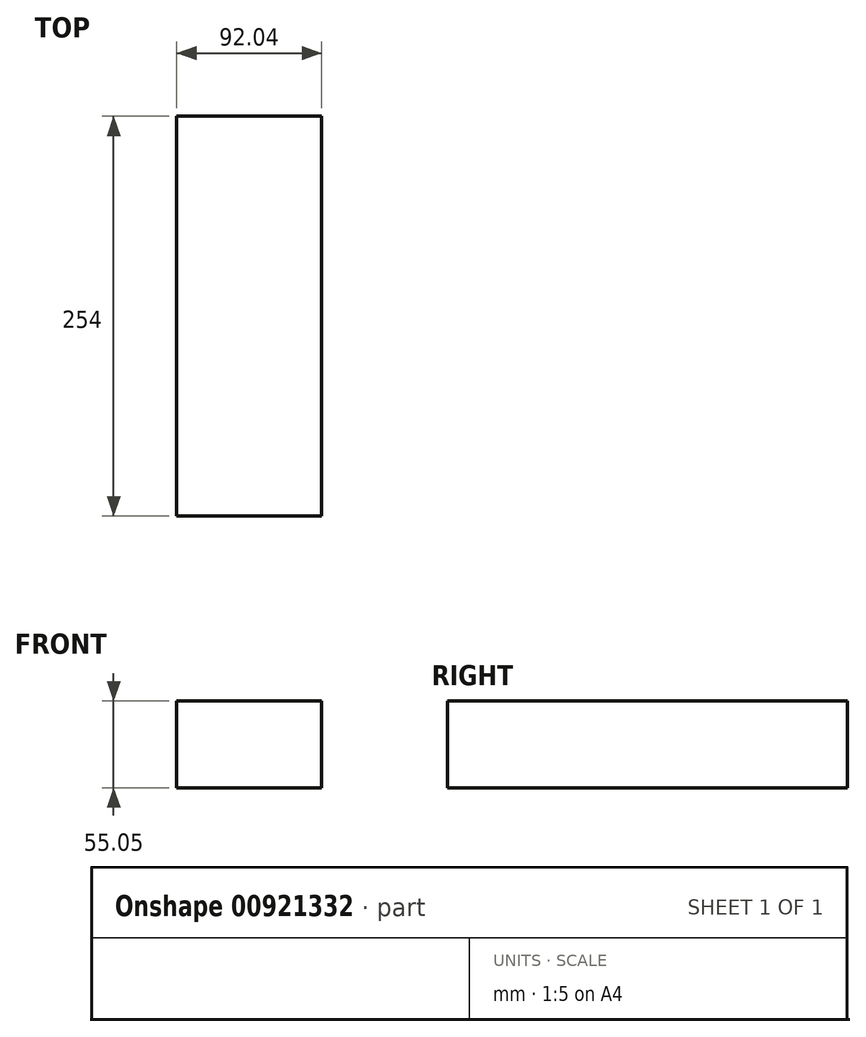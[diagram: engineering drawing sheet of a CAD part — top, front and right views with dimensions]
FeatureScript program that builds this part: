
annotation { "Feature Type Name" : "Feature", "Feature Type Description" : "" }
export const myFeature = defineFeature(function(context is Context, id is Id, definition is map)
    precondition{}
    {
        {
            var Q0;
            Q0=qCreatedBy(makeId("Front.planeOp"),FACE);
            var sketch = newSketch(context, id + "F0", { "sketchPlane" : qUnion([Q0])});
            skLineSegment(sketch, "E0.bottom", {"start": v(-38.95, 36.25) * mm, "end": v(53.09, 36.25) * mm});
            skLineSegment(sketch, "E0.top", {"start": v(-38.95, -18.8) * mm, "end": v(53.09, -18.8) * mm});
            skLineSegment(sketch, "E0.left", {"start": v(-38.95, 36.25) * mm, "end": v(-38.95, -18.8) * mm});
            skLineSegment(sketch, "E0.right", {"start": v(53.09, 36.25) * mm, "end": v(53.09, -18.8) * mm});
            skSolve(sketch);
        }
        {
            var Q0;
            Q0=makeQuery(id+"F0.imprint","IMPRINT",FACE,{"disambiguationData":[TD([[makeQuery(id+"F0.imprint","IMPRINT",EDGE,{"derivedFrom":sQuery(id+"F0.wireOp",EDGE,"E0.bottom")}),-1.0]])]});
            extrude(context, id + "F1", {"entities" : qUnion([Q0]), "depth" : 254 * mm, "offsetDistance" : 25.4 * mm});
        }
    });
